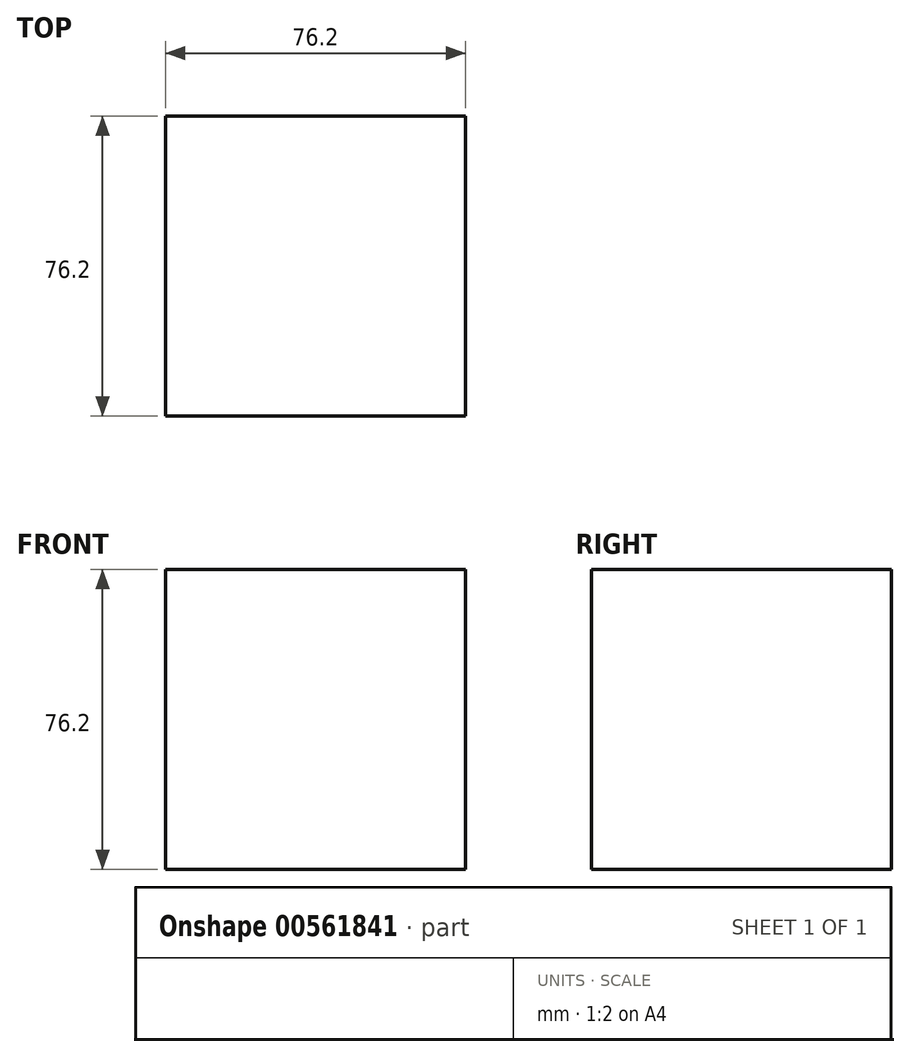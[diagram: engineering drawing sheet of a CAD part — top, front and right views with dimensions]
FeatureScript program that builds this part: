
annotation { "Feature Type Name" : "Feature", "Feature Type Description" : "" }
export const myFeature = defineFeature(function(context is Context, id is Id, definition is map)
    precondition{}
    {
        {
            var Q0;
            Q0=qCreatedBy(makeId("Front.planeOp"),FACE);
            var sketch = newSketch(context, id + "F0", { "sketchPlane" : qUnion([Q0])});
            skLineSegment(sketch, "E0.bottom", {"start": v(-31.28, -25.97) * mm, "end": v(44.92, -25.97) * mm});
            skLineSegment(sketch, "E0.top", {"start": v(-31.28, 50.23) * mm, "end": v(44.92, 50.23) * mm});
            skLineSegment(sketch, "E0.left", {"start": v(-31.28, -25.97) * mm, "end": v(-31.28, 50.23) * mm});
            skLineSegment(sketch, "E0.right", {"start": v(44.92, -25.97) * mm, "end": v(44.92, 50.23) * mm});
            skSolve(sketch);
        }
        {
            var Q0;
            Q0=makeQuery(id+"F0.imprint","IMPRINT",FACE,{"disambiguationData":[TD([[makeQuery(id+"F0.imprint","IMPRINT",EDGE,{"derivedFrom":sQuery(id+"F0.wireOp",EDGE,"E0.bottom")}),1.0]])]});
            extrude(context, id + "F1", {"entities" : qUnion([Q0]), "depth" : 76.2 * mm, "offsetDistance" : 25.4 * mm});
        }
    });
